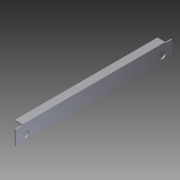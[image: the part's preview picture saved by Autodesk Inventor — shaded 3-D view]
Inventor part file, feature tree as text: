
AUTODESK INVENTOR PART (.ipt)
format: ipt  version: 2012 (Build 160160000, 160)  size: 99,840 bytes
history: native  units: in
note: dims shown in document units (in); Inventor stores cm internally (conversion verified against a paired STEP export)
features: extrude x3, sketch x3
ambient origin geometry x8: Origin, YZ Plane, XZ Plane, XY Plane, X Axis, Y Axis, Z Axis, Center Point
bodies: Solid1 (feature_tree)
feature tree (6):
  extrude  "Extrusion1"  Depth=1.0in
  extrude  "Extrusion2"  Depth=0.125in
  extrude  "Extrusion3"  Depth=0.875in
  sketch  "Sketch1"  dims[d0=2.0in d1=1.0in]
  sketch  "Sketch2"  dims[d2=0.125in d3=0.125in]
  sketch  "Sketch3"  dims[d4=20.0in d5=0.0in d6=0.875in d7=1.25in d8=1.25in d11=20.0in d12=0.0in d13=0.875in d14=0.125in d15=0.0in d16=0.875in d17=1.25in d18=1.25in]
